# Revit family: 1 SOUND_Tower_Wall Bracket Mounted
name_source: partatom
category: Communication Devices
units: mm (PartAtom-declared; Revit-internal decimal feet)

## family parameters
Cut with Voids When Loaded = No
Host = Face
Maintain Annotation Orientation = No
Part Type = Normal
Room Calculation Point = No
Round Connector Dimension = Use Diameter
Shared = No

## types (2) — shared parameters
Bandwidth = 105 Hz - 18 kHz (-6 dB)
Category = Speaker
Connectors = (4) NL4, 1+1-front speakers, 2+2-rear speakers, each allowing for audio inputs and linking
Construction = Finland birch plywood (phenolic glue), polyurea, clear matte salt and UV resistant coating, 316 stainless steel hardware, 3D spacer mesh fabric
Default Elevation = 2438.40 mm
Manufacturer = 1 SOUND
Rigging = Proprietary rigging elemants and fly bars -3 deg, 0 deg, +3 deg, +6 deg, +9 deg; (14) available M6 points
URL = https://www.1-sound.com

## per-type parameters (varying)
| type | Accessory Used | Dimensions (HxWxD) | Impedance | Model | Power | Speaker Model | Wall Mount Model | Weight |
| LCC84 with Wall Bracket | LCC84 Wall Bracket | 878.00mm x 160.00mm x 240.00mm | 8Ω front speakers, 12Ω rear speakers | LCC84 | 1600 watts front + 800 watts rear (continuous), 800 watts + 400 watts (AES) | 1 SOUND_Tower : LCC84 | 1 SOUND_Tower Wall Mount : Wall Mount LCC84 | 19.5 kg |
| LCC44 with Wall Bracket | LCC44 Wall Bracket | 452.00mm x 160.00mm x 240.00mm | 16Ω front speakers, 24Ω rear speakers | LCC44 | 800 watts front + 400 watts rear (continuous), 400 watts + 200 watts (AES) | 1 SOUND_Tower : LCC44 | 1 SOUND_Tower Wall Mount : Wall Mount LCC44 | 10 kg |

## geometry (parser evidence)
native form markers: Sweep x13
no freeform markers — native parametric forms only
